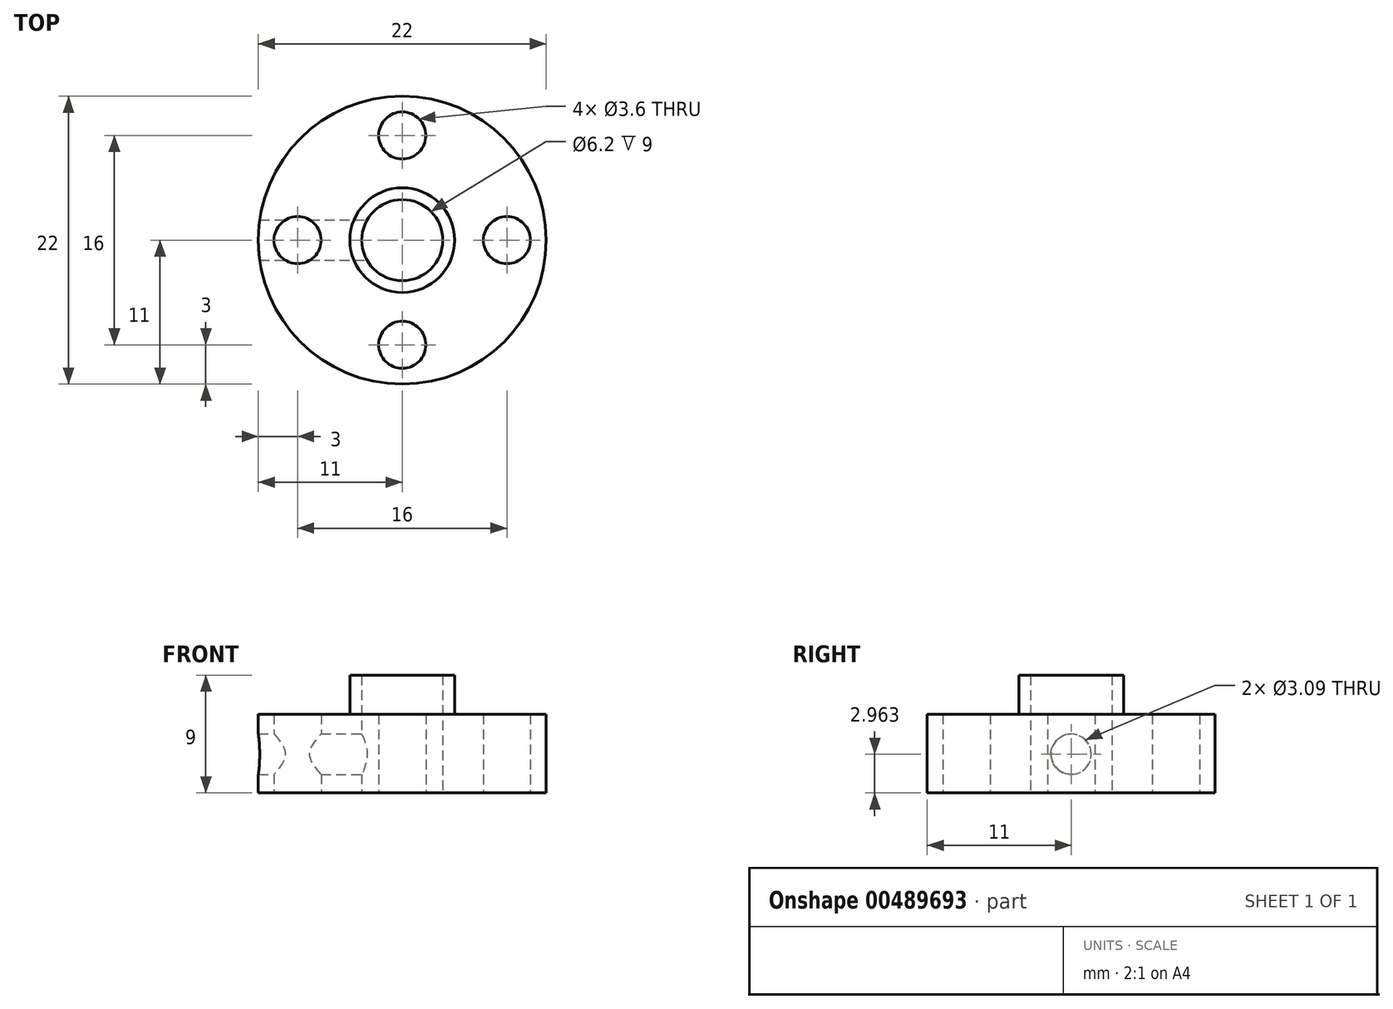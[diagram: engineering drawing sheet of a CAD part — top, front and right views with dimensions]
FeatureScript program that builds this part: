
annotation { "Feature Type Name" : "Feature", "Feature Type Description" : "" }
export const myFeature = defineFeature(function(context is Context, id is Id, definition is map)
    precondition{}
    {
        {
            var Q0;
            Q0=qCreatedBy(makeId("Top.planeOp"),FACE);
            var sketch = newSketch(context, id + "F0", { "sketchPlane" : qUnion([Q0])});
            skCircle(sketch, "E0", {"center": v(0, 0) * mm, "radius": 11 * mm});
            skCircle(sketch, "E1", {"center": v(0, 0) * mm, "radius": 4 * mm});
            skCircle(sketch, "E2", {"center": v(0, 8) * mm, "radius": 1.8 * mm});
            skCircle(sketch, "E3", {"center": v(0, 0) * mm, "radius": 3.1 * mm});
            skCircle(sketch, "E4.1.0", {"center": v(-8, 0) * mm, "radius": 1.8 * mm});
            skCircle(sketch, "E4.2.0", {"center": v(0, -8) * mm, "radius": 1.8 * mm});
            skCircle(sketch, "E4.3.0", {"center": v(8, 0) * mm, "radius": 1.8 * mm});
            skSolve(sketch);
        }
        {
            var Q0;
            Q0=makeQuery(id+"F0.imprint","IMPRINT",FACE,{"disambiguationData":[TD([[makeQuery(id+"F0.imprint","IMPRINT",EDGE,{"derivedFrom":sQuery(id+"F0.wireOp",EDGE,"E0")}),1.0]])]});
            extrude(context, id + "F1", {"entities" : qUnion([Q0]), "depth" : 6 * mm});
        }
        {
            var Q0;
            Q0=makeQuery(id+"F0.imprint","IMPRINT",FACE,{"disambiguationData":[TD([[makeQuery(id+"F0.imprint","IMPRINT",EDGE,{"derivedFrom":sQuery(id+"F0.wireOp",EDGE,"E1")}),1.0]])]});
            extrude(context, id + "F2", {"entities" : qUnion([Q0]), "operationType" : NewBodyOperationType.ADD, "depth" : 9 * mm});
        }
        {
            var Q0;
            Q0=qCreatedBy(makeId("Right.planeOp"),FACE);
            var sketch = newSketch(context, id + "F3", { "sketchPlane" : qUnion([Q0])});
            skCircle(sketch, "E5", {"center": v(0, 2.96) * mm, "radius": 1.54 * mm});
            skSolve(sketch);
        }
        {
            var Q0;
            Q0 = qSketchRegion(id + "F3", true);
            extrude(context, id + "F4", {"entities" : qUnion([Q0]), "operationType" : NewBodyOperationType.REMOVE, "endBound" : BoundingType.THROUGH_ALL, "oppositeDirection" : true, "depth" : 25 * mm});
        }
    });
